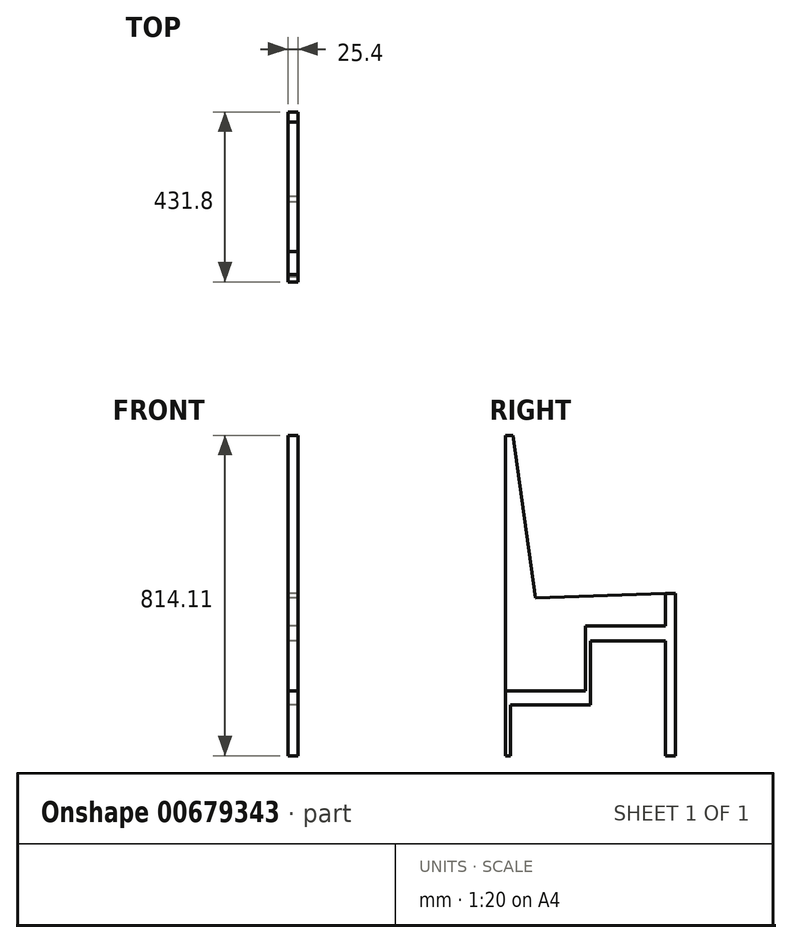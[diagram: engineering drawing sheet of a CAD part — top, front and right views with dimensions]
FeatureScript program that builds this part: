
annotation { "Feature Type Name" : "Feature", "Feature Type Description" : "" }
export const myFeature = defineFeature(function(context is Context, id is Id, definition is map)
    precondition{}
    {
        {
            var Q0;
            Q0=qCreatedBy(makeId("Right.planeOp"),FACE);
            var sketch = newSketch(context, id + "F0", { "sketchPlane" : qUnion([Q0])});
            skLineSegment(sketch, "E0", {"start": v(0, 0) * mm, "end": v(0, 165.1) * mm});
            skLineSegment(sketch, "E1", {"start": v(203.2, 165.1) * mm, "end": v(0, 165.1) * mm});
            skLineSegment(sketch, "E2", {"start": v(203.2, 165.1) * mm, "end": v(203.2, 330.2) * mm});
            skLineSegment(sketch, "E3", {"start": v(203.2, 330.2) * mm, "end": v(406.4, 330.2) * mm});
            skLineSegment(sketch, "E4", {"start": v(612.73, 412.75) * mm, "end": v(612.73, 0) * mm, "construction": true});
            skLineSegment(sketch, "E5", {"start": v(406.4, 330.2) * mm, "end": v(406.4, 0) * mm});
            skLineSegment(sketch, "E6", {"start": v(0, 165.1) * mm, "end": v(-965.57, 165.1) * mm, "construction": true});
            skLineSegment(sketch, "E7", {"start": v(406.4, 0) * mm, "end": v(0, 0) * mm});
            skLineSegment(sketch, "E8", {"start": v(612.73, 0) * mm, "end": v(406.4, 0) * mm, "construction": true});
            skLineSegment(sketch, "E9", {"start": v(406.4, 330.2) * mm, "end": v(406.4, 412.75) * mm});
            skLineSegment(sketch, "E10", {"start": v(406.4, 412.75) * mm, "end": v(0, 412.75) * mm});
            skLineSegment(sketch, "E11", {"start": v(0, 412.75) * mm, "end": v(0, 165.1) * mm});
            skLineSegment(sketch, "E12", {"start": v(406.4, 412.75) * mm, "end": v(612.73, 412.75) * mm, "construction": true});
            skLineSegment(sketch, "E13", {"start": v(203.2, 330.2) * mm, "end": v(203.2, 515.87) * mm, "construction": true});
            skLineSegment(sketch, "E14", {"start": v(203.2, 515.87) * mm, "end": v(-40.5, 515.87) * mm, "construction": true});
            skLineSegment(sketch, "E15", {"start": v(-40.5, 515.87) * mm, "end": v(-40.5, 165.1) * mm, "construction": true});
            skLineSegment(sketch, "E16", {"start": v(-40.5, 165.1) * mm, "end": v(0, 165.1) * mm});
            skLineSegment(sketch, "E17", {"start": v(406.4, 0) * mm, "end": v(431.8, 0) * mm});
            skLineSegment(sketch, "E18", {"start": v(431.8, 412.75) * mm, "end": v(406.4, 412.75) * mm});
            skLineSegment(sketch, "E19", {"start": v(431.8, 412.75) * mm, "end": v(431.8, 0) * mm});
            skLineSegment(sketch, "E20.left", {"start": v(0, 203.2) * mm, "end": v(0, 330.2) * mm});
            skLineSegment(sketch, "E21.bottom", {"start": v(215.98, 0) * mm, "end": v(406.4, 0) * mm});
            skLineSegment(sketch, "E21.top", {"start": v(215.98, 292.1) * mm, "end": v(406.4, 292.1) * mm});
            skLineSegment(sketch, "E21.left", {"start": v(215.98, 0) * mm, "end": v(215.98, 292.1) * mm});
            skLineSegment(sketch, "E21.right", {"start": v(406.4, 0) * mm, "end": v(406.4, 292.1) * mm});
            skLineSegment(sketch, "E22.bottom", {"start": v(11.84, 0) * mm, "end": v(203.2, 0) * mm});
            skLineSegment(sketch, "E22.top", {"start": v(11.84, 128.87) * mm, "end": v(203.2, 128.87) * mm});
            skLineSegment(sketch, "E22.left", {"start": v(11.84, 0) * mm, "end": v(11.84, 128.87) * mm});
            skLineSegment(sketch, "E23", {"start": v(18.26, 814.1) * mm, "end": v(76.29, 401.22) * mm});
            skLineSegment(sketch, "E24", {"start": v(0, 412.75) * mm, "end": v(0, 814.1) * mm});
            skLineSegment(sketch, "E25", {"start": v(203.2, 128.87) * mm, "end": v(215.98, 128.87) * mm});
            skLineSegment(sketch, "E26", {"start": v(203.2, 330.2) * mm, "end": v(-965.57, 330.2) * mm, "construction": true});
            skLineSegment(sketch, "E27", {"start": v(18.26, 814.1) * mm, "end": v(0, 814.1) * mm});
            skLineSegment(sketch, "E28", {"start": v(406.4, 412.75) * mm, "end": v(76.29, 401.22) * mm});
            skSolve(sketch);
        }
        {
            var Q0;
            {var subQ9=sQuery(id+"F0.wireOp",EDGE,"E1");Q0=makeQuery(id+"F0.imprint","IMPRINT",FACE,{"disambiguationData":[TD([[makeQuery(id+"F0.imprint","IMPRINT",EDGE,{"derivedFrom":subQ9}),-1.0]])]});}
            var Q1;
            {var subQ0=sQuery(id+"F0.wireOp",EDGE,"T97KkR0k-YW4B-Y2rO-eG4X-VHP36lvGthJP");Q1=makeQuery(id+"F0.imprint","IMPRINT",FACE,{"disambiguationData":[TD([[makeQuery(id+"F0.imprint","IMPRINT",EDGE,{"derivedFrom":subQ0}),1.0]])]});}
            var Q2;
            {var subQ2=sQuery(id+"F0.wireOp",EDGE,"T97KkR0k-YW4B-Y2rO-eG4X-VHP36lvGthJP");Q2=makeQuery(id+"F0.imprint","IMPRINT",FACE,{"disambiguationData":[TD([[makeQuery(id+"F0.imprint","IMPRINT",EDGE,{"derivedFrom":subQ2}),-1.0]])]});}
            var Q3;
            {var subQ0=sQuery(id+"F0.wireOp",EDGE,"E24");Q3=makeQuery(id+"F0.imprint","IMPRINT",FACE,{"disambiguationData":[TD([[makeQuery(id+"F0.imprint","IMPRINT",EDGE,{"derivedFrom":subQ0}),-1.0]])]});}
            extrude(context, id + "F1", {"entities" : qUnion([Q0, Q1, Q2, Q3]), "depth" : 25.4 * mm, "offsetDistance" : 25.4 * mm});
        }
        {
            var Q0;
            Q0=makeQuery(id+"F0.imprint","IMPRINT",FACE,{"disambiguationData":[TD([[makeQuery(id+"F0.imprint","IMPRINT",EDGE,{"derivedFrom":sQuery(id+"F0.wireOp",EDGE,"E5")}),1.0]])]});
            var Q1;
            Q1=makeQuery(id+"F0.imprint","IMPRINT",FACE,{"disambiguationData":[TD([[makeQuery(id+"F0.imprint","IMPRINT",EDGE,{"derivedFrom":sQuery(id+"F0.wireOp",EDGE,"E0")}),-1.0]])]});
            extrude(context, id + "F2", {"entities" : qUnion([Q0, Q1]), "depth" : 25.4 * mm, "offsetDistance" : 25.4 * mm});
        }
    });
